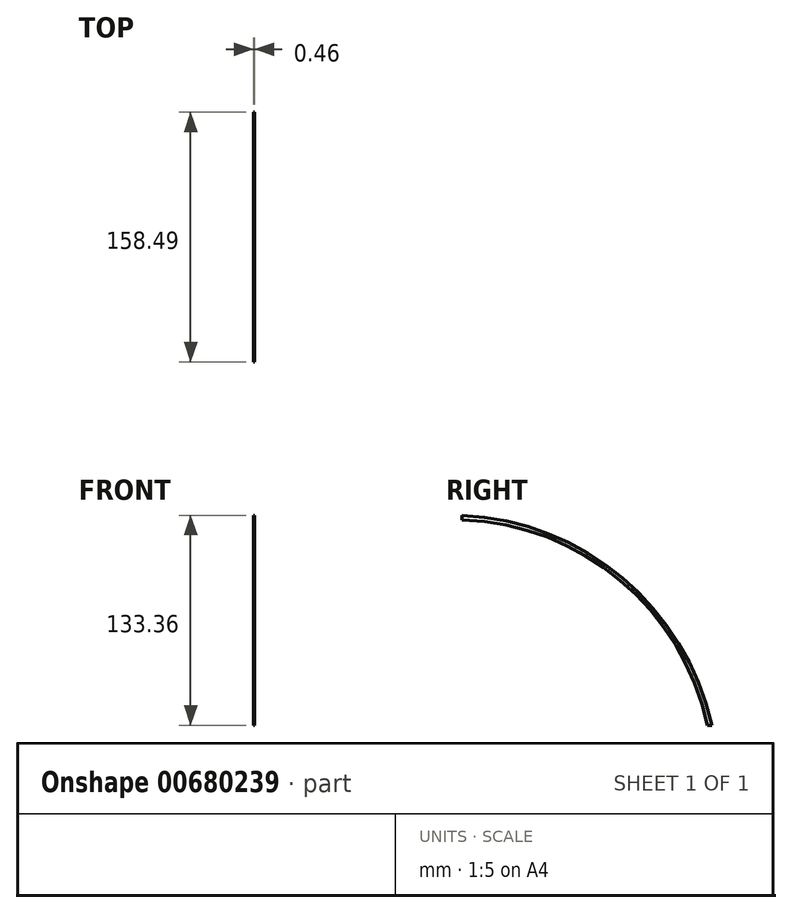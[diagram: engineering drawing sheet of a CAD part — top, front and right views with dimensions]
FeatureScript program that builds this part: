
annotation { "Feature Type Name" : "Feature", "Feature Type Description" : "" }
export const myFeature = defineFeature(function(context is Context, id is Id, definition is map)
    precondition{}
    {
        {
            var Q0;
            Q0=qCreatedBy(makeId("Right.planeOp"),FACE);
            var sketch = newSketch(context, id + "F0", { "sketchPlane" : qUnion([Q0])});
            skArc(sketch, "E0", {"start": v(0, 0) * mm, "mid": v(-55.39, 92.07) * mm, "end": v(-155.7, 130.56) * mm});
            skLineSegment(sketch, "E1", {"start": v(-155.7, 130.56) * mm, "end": v(-155.7, 133.36) * mm});
            skLineSegment(sketch, "E2", {"start": v(0, 0) * mm, "end": v(2.8, 0) * mm});
            skArc(sketch, "E3", {"start": v(2.8, 0) * mm, "mid": v(-53.88, 93.51) * mm, "end": v(-155.7, 133.36) * mm});
            skSolve(sketch);
        }
        {
            var Q0;
            Q0 = qSketchRegion(id + "F0", true);
            extrude(context, id + "F1", {"entities" : qUnion([Q0]), "oppositeDirection" : true, "depth" : 11.6 / 50.8 * mm, "offsetDistance" : 25.4 * mm, "hasSecondDirection" : true, "secondDirectionOppositeDirection" : false, "secondDirectionDepth" : 11.6 / 50.8 * mm});
        }
        {
            var Q0;
            Q0=qCreatedBy(makeId("Top.planeOp"),FACE);
            var sketch = newSketch(context, id + "F2", { "sketchPlane" : qUnion([Q0])});
            skArc(sketch, "E4", {"start": v(-147.2, -137.4) * mm, "mid": v(-141.81, -150.47) * mm, "end": v(-128.68, -155.7) * mm});
            skLineSegment(sketch, "E5", {"start": v(-147.2, -137.4) * mm, "end": v(-161.34, -137.4) * mm});
            skLineSegment(sketch, "E6", {"start": v(-161.34, -137.4) * mm, "end": v(-161.34, -161.33) * mm});
            skLineSegment(sketch, "E7", {"start": v(-161.34, -161.33) * mm, "end": v(-129.24, -161.33) * mm});
            skLineSegment(sketch, "E8", {"start": v(-129.24, -161.33) * mm, "end": v(-128.68, -155.7) * mm});
            skLineSegment(sketch, "E9.MirrorCS", {"start": v(129.24, -161.33) * mm, "end": v(128.68, -155.7) * mm});
            skLineSegment(sketch, "E10.MirrorCS", {"start": v(161.34, -137.4) * mm, "end": v(161.34, -161.33) * mm});
            skArc(sketch, "E11.MirrorCS", {"start": v(147.2, -137.4) * mm, "mid": v(141.81, -150.47) * mm, "end": v(128.68, -155.7) * mm});
            skLineSegment(sketch, "E12.MirrorCS", {"start": v(161.34, -161.33) * mm, "end": v(129.24, -161.33) * mm});
            skLineSegment(sketch, "E13.MirrorCS", {"start": v(147.2, -137.4) * mm, "end": v(161.34, -137.4) * mm});
            skSolve(sketch);
        }
        {
            var Q0;
            Q0 = qSketchRegion(id + "F2", true);
            extrude(context, id + "F3", {"entities" : qUnion([Q0]), "operationType" : NewBodyOperationType.REMOVE, "depth" : 186.18 * mm, "offsetDistance" : 25.4 * mm});
        }
    });
